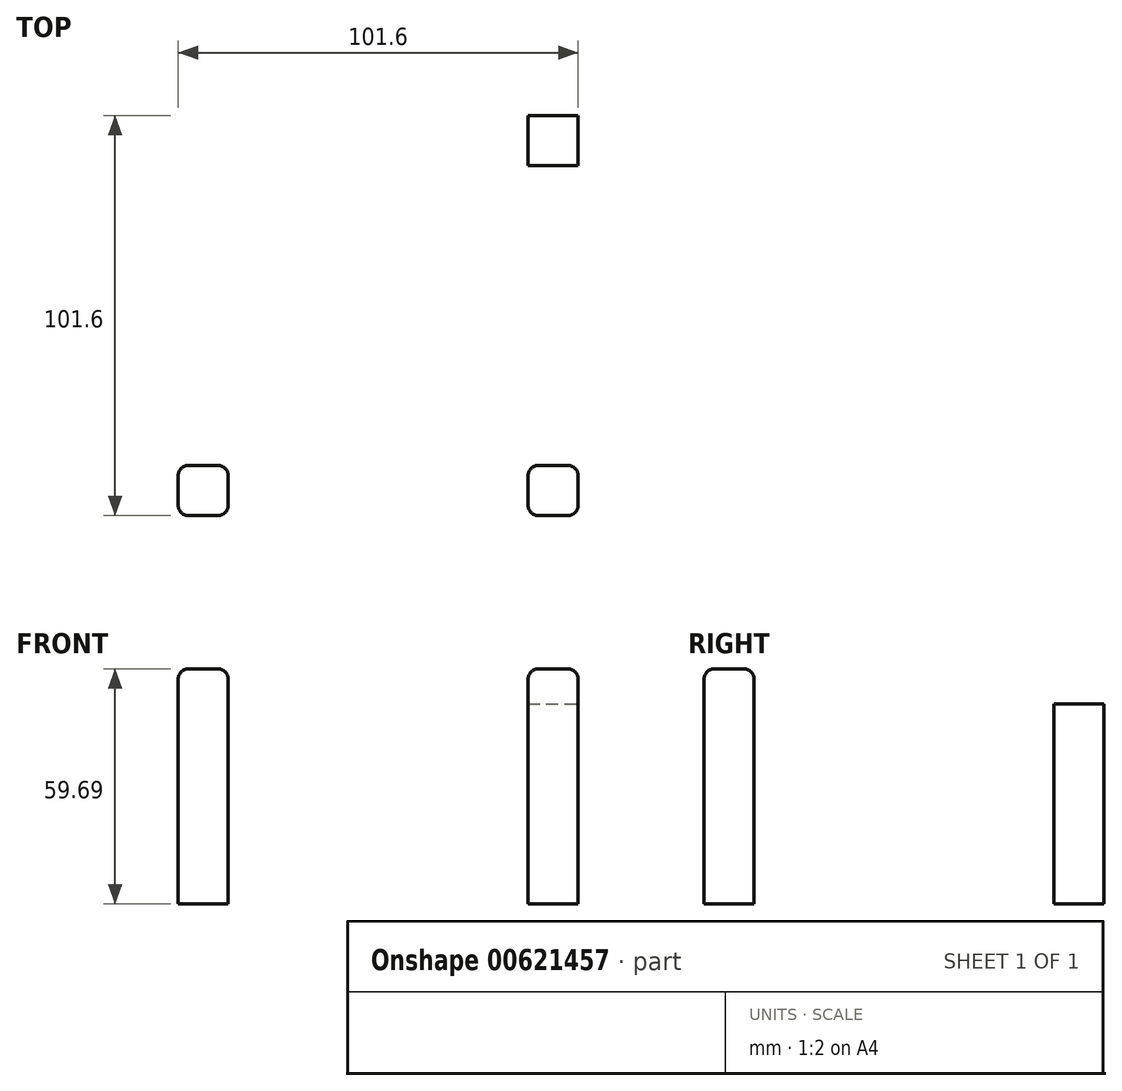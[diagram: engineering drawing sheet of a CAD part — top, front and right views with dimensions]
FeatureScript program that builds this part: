
annotation { "Feature Type Name" : "Feature", "Feature Type Description" : "" }
export const myFeature = defineFeature(function(context is Context, id is Id, definition is map)
    precondition{}
    {
        {
            var Q0;
            Q0=qCreatedBy(makeId("Top.planeOp"),FACE);
            var sketch = newSketch(context, id + "F0", { "sketchPlane" : qUnion([Q0])});
            skLineSegment(sketch, "E0.bottom", {"start": v(0, 0) * mm, "end": v(101.6, 0) * mm});
            skLineSegment(sketch, "E0.top", {"start": v(0, 101.6) * mm, "end": v(101.6, 101.6) * mm});
            skLineSegment(sketch, "E0.left", {"start": v(0, 0) * mm, "end": v(0, 101.6) * mm});
            skLineSegment(sketch, "E0.right", {"start": v(101.6, 0) * mm, "end": v(101.6, 101.6) * mm});
            skLineSegment(sketch, "E1.bottom", {"start": v(0, 101.6) * mm, "end": v(12.7, 101.6) * mm});
            skLineSegment(sketch, "E1.top", {"start": v(0, 88.9) * mm, "end": v(12.7, 88.9) * mm});
            skLineSegment(sketch, "E1.left", {"start": v(0, 101.6) * mm, "end": v(0, 88.9) * mm});
            skLineSegment(sketch, "E1.right", {"start": v(12.7, 101.6) * mm, "end": v(12.7, 88.9) * mm});
            skLineSegment(sketch, "E2.bottom", {"start": v(12.7, 0) * mm, "end": v(0, 0) * mm});
            skLineSegment(sketch, "E2.top", {"start": v(12.7, 12.7) * mm, "end": v(0, 12.7) * mm});
            skLineSegment(sketch, "E2.left", {"start": v(12.7, 0) * mm, "end": v(12.7, 12.7) * mm});
            skLineSegment(sketch, "E2.right", {"start": v(0, 0) * mm, "end": v(0, 12.7) * mm});
            skLineSegment(sketch, "E3.bottom", {"start": v(101.6, 12.7) * mm, "end": v(88.9, 12.7) * mm});
            skLineSegment(sketch, "E3.top", {"start": v(101.6, 0) * mm, "end": v(88.9, 0) * mm});
            skLineSegment(sketch, "E3.left", {"start": v(101.6, 12.7) * mm, "end": v(101.6, 0) * mm});
            skLineSegment(sketch, "E3.right", {"start": v(88.9, 12.7) * mm, "end": v(88.9, 0) * mm});
            skLineSegment(sketch, "E4.bottom", {"start": v(88.9, 88.9) * mm, "end": v(101.6, 88.9) * mm});
            skLineSegment(sketch, "E4.top", {"start": v(88.9, 101.6) * mm, "end": v(101.6, 101.6) * mm});
            skLineSegment(sketch, "E4.left", {"start": v(88.9, 88.9) * mm, "end": v(88.9, 101.6) * mm});
            skLineSegment(sketch, "E4.right", {"start": v(101.6, 88.9) * mm, "end": v(101.6, 101.6) * mm});
            skSolve(sketch);
        }
        {
            var Q0;
            Q0=makeQuery(id+"F0.imprint","IMPRINT",FACE,{"disambiguationData":[TD([[makeQuery(id+"F0.imprint","IMPRINT",EDGE,{"derivedFrom":sQuery(id+"F0.wireOp",EDGE,"E0.bottom")}),1.0]])]});
            var Q1;
            Q1=makeQuery(id+"F0.imprint","IMPRINT",FACE,{"disambiguationData":[TD([[makeQuery(id+"F0.imprint","IMPRINT",EDGE,{"derivedFrom":sQuery(id+"F0.wireOp",EDGE,"E1.bottom")}),-1.0]])]});
            var Q2;
            Q2=makeQuery(id+"F0.imprint","IMPRINT",FACE,{"disambiguationData":[TD([[makeQuery(id+"F0.imprint","IMPRINT",EDGE,{"derivedFrom":sQuery(id+"F0.wireOp",EDGE,"E4.bottom")}),1.0]])]});
            var Q3;
            Q3=makeQuery(id+"F0.imprint","IMPRINT",FACE,{"disambiguationData":[TD([[makeQuery(id+"F0.imprint","IMPRINT",EDGE,{"derivedFrom":sQuery(id+"F0.wireOp",EDGE,"E3.bottom")}),1.0]])]});
            var Q4;
            Q4=makeQuery(id+"F0.imprint","IMPRINT",FACE,{"disambiguationData":[TD([[makeQuery(id+"F0.imprint","IMPRINT",EDGE,{"derivedFrom":sQuery(id+"F0.wireOp",EDGE,"E2.bottom")}),-1.0]])]});
            extrude(context, id + "F1", {"entities" : qUnion([Q0, Q1, Q2, Q3, Q4]), "oppositeDirection" : true, "depth" : 50.8 * mm, "offsetDistance" : 25.4 * mm});
        }
        {
            var Q0;
            Q0=makeQuery(id+"F0.imprint","IMPRINT",FACE,{"disambiguationData":[TD([[makeQuery(id+"F0.imprint","IMPRINT",EDGE,{"derivedFrom":sQuery(id+"F0.wireOp",EDGE,"E0.bottom")}),1.0]])]});
            extrude(context, id + "F2", {"entities" : qUnion([Q0]), "operationType" : NewBodyOperationType.ADD, "depth" : 8.9 * mm, "offsetDistance" : 25.4 * mm});
        }
        {
            var Q0;
            Q0=makeQuery(id+"F2.opExtrude","CAP_EDGE",EDGE,{"disambiguationData":[OSD([sQuery(id+"F0.wireOp",EDGE,"E0.top")])],"isStart":false});
            var Q1;
            Q1=makeQuery(id+"F2.opExtrude","CAP_EDGE",EDGE,{"disambiguationData":[OSD([sQuery(id+"F0.wireOp",EDGE,"E0.left")])],"isStart":false});
            var Q2;
            Q2=makeQuery(id+"F2.opExtrude","CAP_EDGE",EDGE,{"disambiguationData":[OSD([sQuery(id+"F0.wireOp",EDGE,"E0.bottom")])],"isStart":false});
            var Q3;
            Q3=makeQuery(id+"F2.opExtrude","CAP_EDGE",EDGE,{"disambiguationData":[OSD([sQuery(id+"F0.wireOp",EDGE,"E4.bottom")])],"isStart":false});
            var Q4;
            Q4=makeQuery(id+"F2.opExtrude","CAP_EDGE",EDGE,{"disambiguationData":[OSD([sQuery(id+"F0.wireOp",EDGE,"E1.top")])],"isStart":false});
            var Q5;
            Q5=makeQuery(id+"F2.opExtrude","CAP_EDGE",EDGE,{"disambiguationData":[OSD([sQuery(id+"F0.wireOp",EDGE,"E2.top")])],"isStart":false});
            var Q6;
            Q6=makeQuery(id+"F2.opExtrude","CAP_EDGE",EDGE,{"disambiguationData":[OSD([sQuery(id+"F0.wireOp",EDGE,"E3.bottom")])],"isStart":false});
            var Q7;
            Q7=makeQuery(id+"F2.opExtrude","CAP_EDGE",EDGE,{"disambiguationData":[OSD([sQuery(id+"F0.wireOp",EDGE,"E0.right")])],"isStart":false});
            var Q8;
            Q8=makeQuery(id+"F2.opExtrude","CAP_EDGE",EDGE,{"disambiguationData":[OSD([sQuery(id+"F0.wireOp",EDGE,"E3.right")])],"isStart":false});
            var Q9;
            Q9=makeQuery(id+"F2.opExtrude","CAP_EDGE",EDGE,{"disambiguationData":[OSD([sQuery(id+"F0.wireOp",EDGE,"E2.left")])],"isStart":false});
            var Q10;
            Q10=makeQuery(id+"F2.opExtrude","CAP_EDGE",EDGE,{"disambiguationData":[OSD([sQuery(id+"F0.wireOp",EDGE,"E1.right")])],"isStart":false});
            var Q11;
            Q11=makeQuery(id+"F2.opExtrude","CAP_EDGE",EDGE,{"disambiguationData":[OSD([sQuery(id+"F0.wireOp",EDGE,"E4.left")])],"isStart":false});
            var Q12;
            Q12=makeQuery(id+"F2.opExtrude","CAP_EDGE",EDGE,{"disambiguationData":[OSD([sQuery(id+"F0.wireOp",EDGE,"E3.right")])],"isStart":true});
            var Q13;
            Q13=makeQuery(id+"F2.opExtrude","CAP_EDGE",EDGE,{"disambiguationData":[OSD([sQuery(id+"F0.wireOp",EDGE,"E3.bottom")])],"isStart":true});
            var Q14;
            Q14=makeQuery(id+"F2.opExtrude","SWEPT_EDGE",EDGE,{"disambiguationData":[OSD([sQuery(id+"F0.wireOp",EDGE,"E3.bottom"),sQuery(id+"F0.wireOp",EDGE,"E3.right")])]});
            var Q15;
            Q15=makeQuery(id+"F2.opExtrude","SWEPT_EDGE",EDGE,{"disambiguationData":[OSD([sQuery(id+"F0.wireOp",EDGE,"E2.top"),sQuery(id+"F0.wireOp",EDGE,"E2.left")])]});
            var Q16;
            Q16=makeQuery(id+"F2.opExtrude","CAP_EDGE",EDGE,{"disambiguationData":[OSD([sQuery(id+"F0.wireOp",EDGE,"E2.top")])],"isStart":true});
            var Q17;
            Q17=makeQuery(id+"F2.opExtrude","CAP_EDGE",EDGE,{"disambiguationData":[OSD([sQuery(id+"F0.wireOp",EDGE,"E2.left")])],"isStart":true});
            var Q18;
            Q18=makeQuery(id+"F2.opExtrude","SWEPT_EDGE",EDGE,{"disambiguationData":[OSD([sQuery(id+"F0.wireOp",EDGE,"E1.top"),sQuery(id+"F0.wireOp",EDGE,"E1.right")])]});
            var Q19;
            Q19=makeQuery(id+"F2.opExtrude","CAP_EDGE",EDGE,{"disambiguationData":[OSD([sQuery(id+"F0.wireOp",EDGE,"E1.right")])],"isStart":true});
            var Q20;
            Q20=makeQuery(id+"F2.opExtrude","CAP_EDGE",EDGE,{"disambiguationData":[OSD([sQuery(id+"F0.wireOp",EDGE,"E1.top")])],"isStart":true});
            var Q21;
            Q21=makeQuery(id+"F2.opExtrude","CAP_EDGE",EDGE,{"disambiguationData":[OSD([sQuery(id+"F0.wireOp",EDGE,"E4.bottom")])],"isStart":true});
            var Q22;
            Q22=makeQuery(id+"F2.opExtrude","SWEPT_EDGE",EDGE,{"disambiguationData":[OSD([sQuery(id+"F0.wireOp",EDGE,"E4.bottom"),sQuery(id+"F0.wireOp",EDGE,"E4.left")])]});
            var Q23;
            Q23=makeQuery(id+"F2.opExtrude","SWEPT_EDGE",EDGE,{"disambiguationData":[OSD([sQuery(id+"F0.wireOp",EDGE,"E0.top"),sQuery(id+"F0.wireOp",EDGE,"E4.top"),sQuery(id+"F0.wireOp",EDGE,"E4.left")])]});
            var Q24;
            Q24=makeQuery(id+"F2.opExtrude","SWEPT_EDGE",EDGE,{"disambiguationData":[OSD([sQuery(id+"F0.wireOp",EDGE,"E0.right"),sQuery(id+"F0.wireOp",EDGE,"E3.bottom"),sQuery(id+"F0.wireOp",EDGE,"E3.left")])]});
            var Q25;
            Q25=makeQuery(id+"F2.opExtrude","SWEPT_EDGE",EDGE,{"disambiguationData":[OSD([sQuery(id+"F0.wireOp",EDGE,"E0.bottom"),sQuery(id+"F0.wireOp",EDGE,"E3.top"),sQuery(id+"F0.wireOp",EDGE,"E3.right")])]});
            var Q26;
            Q26=makeQuery(id+"F2.opExtrude","SWEPT_EDGE",EDGE,{"disambiguationData":[OSD([sQuery(id+"F0.wireOp",EDGE,"E0.bottom"),sQuery(id+"F0.wireOp",EDGE,"E2.bottom"),sQuery(id+"F0.wireOp",EDGE,"E2.left")])]});
            var Q27;
            Q27=makeQuery(id+"F2.opExtrude","SWEPT_EDGE",EDGE,{"disambiguationData":[OSD([sQuery(id+"F0.wireOp",EDGE,"E0.left"),sQuery(id+"F0.wireOp",EDGE,"E2.top"),sQuery(id+"F0.wireOp",EDGE,"E2.right")])]});
            var Q28;
            Q28=makeQuery(id+"F2.opExtrude","SWEPT_EDGE",EDGE,{"disambiguationData":[OSD([sQuery(id+"F0.wireOp",EDGE,"E0.left"),sQuery(id+"F0.wireOp",EDGE,"E1.top"),sQuery(id+"F0.wireOp",EDGE,"E1.left")])]});
            var Q29;
            Q29=makeQuery(id+"F2.opExtrude","SWEPT_EDGE",EDGE,{"disambiguationData":[OSD([sQuery(id+"F0.wireOp",EDGE,"E0.top"),sQuery(id+"F0.wireOp",EDGE,"E1.bottom"),sQuery(id+"F0.wireOp",EDGE,"E1.right")])]});
            var Q30;
            Q30=makeQuery(id+"F2.opExtrude","SWEPT_EDGE",EDGE,{"disambiguationData":[OSD([sQuery(id+"F0.wireOp",EDGE,"E0.right"),sQuery(id+"F0.wireOp",EDGE,"E4.bottom"),sQuery(id+"F0.wireOp",EDGE,"E4.right")])]});
            fillet(context, id + "F3", {"entities" : qUnion([Q0, Q1, Q2, Q3, Q4, Q5, Q6, Q7, Q8, Q9, Q10, Q11, Q12, Q13, Q14, Q15, Q16, Q17, Q18, Q19, Q20, Q21, Q22, Q23, Q24, Q25, Q26, Q27, Q28, Q29, Q30]), "radius" : 2.54 * mm, "tangentPropagation" : true, "allowEdgeOverflow" : false});
        }
    });
